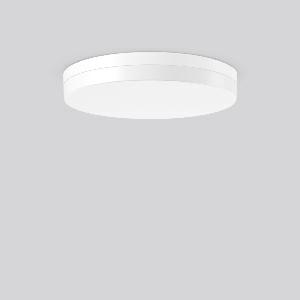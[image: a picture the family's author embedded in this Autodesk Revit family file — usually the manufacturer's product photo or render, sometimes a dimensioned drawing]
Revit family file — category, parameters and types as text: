
# Revit family: flat_slim_round_312634_002_730_4618
name_source: partatom
category: Lighting Fixtures
units: mm (PartAtom-declared; Revit-internal decimal feet)

## family parameters
Cut with Voids When Loaded = No
Host = Face
Light Source = No
Part Type = Normal
Room Calculation Point = No
Round Connector Dimension = Use Diameter
Shared = No

## types (1)
- MultiLumen 1 830 (1 x LED Modul 830, 3450 lm, 3000)
    Apparent Load = 26 VA
    CIE Flux Codes = 40 71 90 84 100
    Color Rendering = 80
    Color Temperature = 3000
    Default Elevation = 1800 mm
    Height = 70 mm
    Lamp = 1 x LED Modul 830
    Lamp Light Flux = 3450 lm
    Lamp count = 1
    Length = 480 mm
    Lifetime = 50000 h
    Luminous efficacy = 133 lm/W
    Manufacturer = RZB
    ModVariant = No
    Model = 312634.002.730
    Mounting Place = Ceiling
    Mounting Type = Surface mounted
    Number of Poles = 1
    OnlyDefault = Yes
    Power Factor = 1
    Product Name = FLAT SLIM round
    Product group = Surface mounted ceiling and wall luminaires
    ProductGroupID = 305
    Protection Class = Protection class I
    Protection Degree = Degree of protection
    RLX_Detail_Level = 1
    RLX_Emergency_Light_Flux = 0 lm
    RLX_Emergency_Type = 0
    RLX_Emergency_Type_DB = No
    RlxData = <blob elided: 21413 chars, md5=f54ac9cb>
    Socket = socket
    Standby Power = 0 W
    System Light Flux = 3450 lm
    System Power = 26 W
    Type Comments = MultiLumen 1 830
    Type Image = 312633.002.jpg
    URL = http://relux.com
    VarID = multilumen_1_830
    Voltage = 0 V
    Weight = 0.00 kg
    Width = 0 mm  [stored 0 ft]

note: [stored X ft] marks values corroborated as IEEE doubles in the binary element streams (Revit-internal decimal feet)

## geometry (parser evidence)
native form markers: Blend x4, Sweep x14
no freeform markers — native parametric forms only
